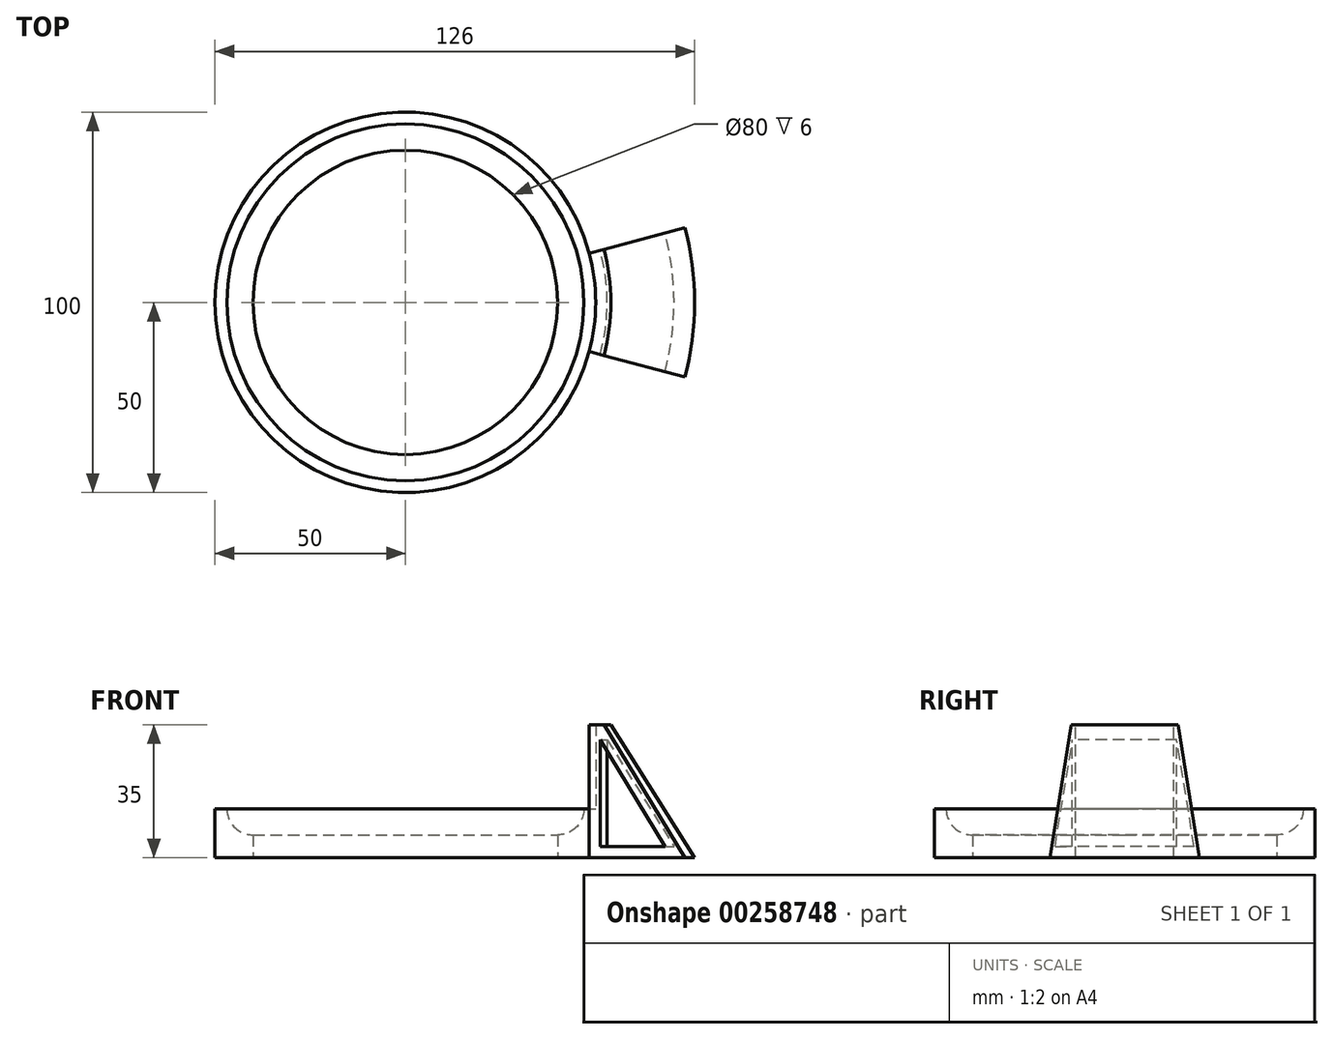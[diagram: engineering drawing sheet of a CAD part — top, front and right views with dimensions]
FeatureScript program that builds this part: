
annotation { "Feature Type Name" : "Feature", "Feature Type Description" : "" }
export const myFeature = defineFeature(function(context is Context, id is Id, definition is map)
    precondition{}
    {
        {
            var Q0;
            Q0=qCreatedBy(makeId("Front.planeOp"),FACE);
            var sketch = newSketch(context, id + "F0", { "sketchPlane" : qUnion([Q0])});
            skLineSegment(sketch, "E0", {"start": v(0, -28.47) * mm, "end": v(0, 44.07) * mm, "construction": true});
            skSolve(sketch);
        }
        {
            var Q0;
            Q0=qCreatedBy(makeId("Front.planeOp"),FACE);
            var sketch = newSketch(context, id + "F1", { "sketchPlane" : qUnion([Q0])});
            skLineSegment(sketch, "E1", {"start": v(40, 0) * mm, "end": v(40, 6) * mm});
            skArc(sketch, "E2", {"start": v(40, 6) * mm, "mid": v(44.88, 8.02) * mm, "end": v(46.9, 12.9) * mm});
            skLineSegment(sketch, "E3", {"start": v(46.9, 12.9) * mm, "end": v(50, 12.9) * mm});
            skLineSegment(sketch, "E4", {"start": v(50, 0) * mm, "end": v(50, 12.9) * mm});
            skLineSegment(sketch, "E5", {"start": v(40, 0) * mm, "end": v(50, 0) * mm});
            skSolve(sketch);
        }
        {
            var Q0;
            Q0 = qSketchRegion(id + "F1", true);
            var Q1;
            Q1=sQuery(id+"F0.wireOp",EDGE,"E0");
            revolve(context, id + "F2", {"entities" : qUnion([Q0]), "axis" : qUnion([Q1]), "revolveType" : RevolveType.FULL});
        }
        {
            var Q0;
            Q0=qCreatedBy(makeId("Front.planeOp"),FACE);
            var sketch = newSketch(context, id + "F3", { "sketchPlane" : qUnion([Q0])});
            skLineSegment(sketch, "E6", {"start": v(50, 0) * mm, "end": v(50, 35) * mm});
            skLineSegment(sketch, "E7", {"start": v(76, 0) * mm, "end": v(50, 0) * mm});
            skLineSegment(sketch, "E8", {"start": v(76, 0) * mm, "end": v(54, 35) * mm});
            skLineSegment(sketch, "E9", {"start": v(54, 35) * mm, "end": v(50, 35) * mm});
            skLineSegment(sketch, "E10.0", {"start": v(70.57, 3) * mm, "end": v(53, 30.95) * mm});
            skLineSegment(sketch, "E10.1", {"start": v(70.57, 3) * mm, "end": v(53, 3) * mm});
            skLineSegment(sketch, "E10.2", {"start": v(53, 3) * mm, "end": v(53, 30.95) * mm});
            skSolve(sketch);
        }
        {
            var Q0;
            Q0 = qSketchRegion(id + "F3", true);
            var Q1;
            Q1=sQuery(id+"F0.wireOp",EDGE,"E0");
            revolve(context, id + "F4", {"operationType" : NewBodyOperationType.ADD, "entities" : qUnion([Q0]), "axis" : qUnion([Q1]), "revolveType" : RevolveType.SYMMETRIC, "angle" : 30 * degree});
        }
    });
